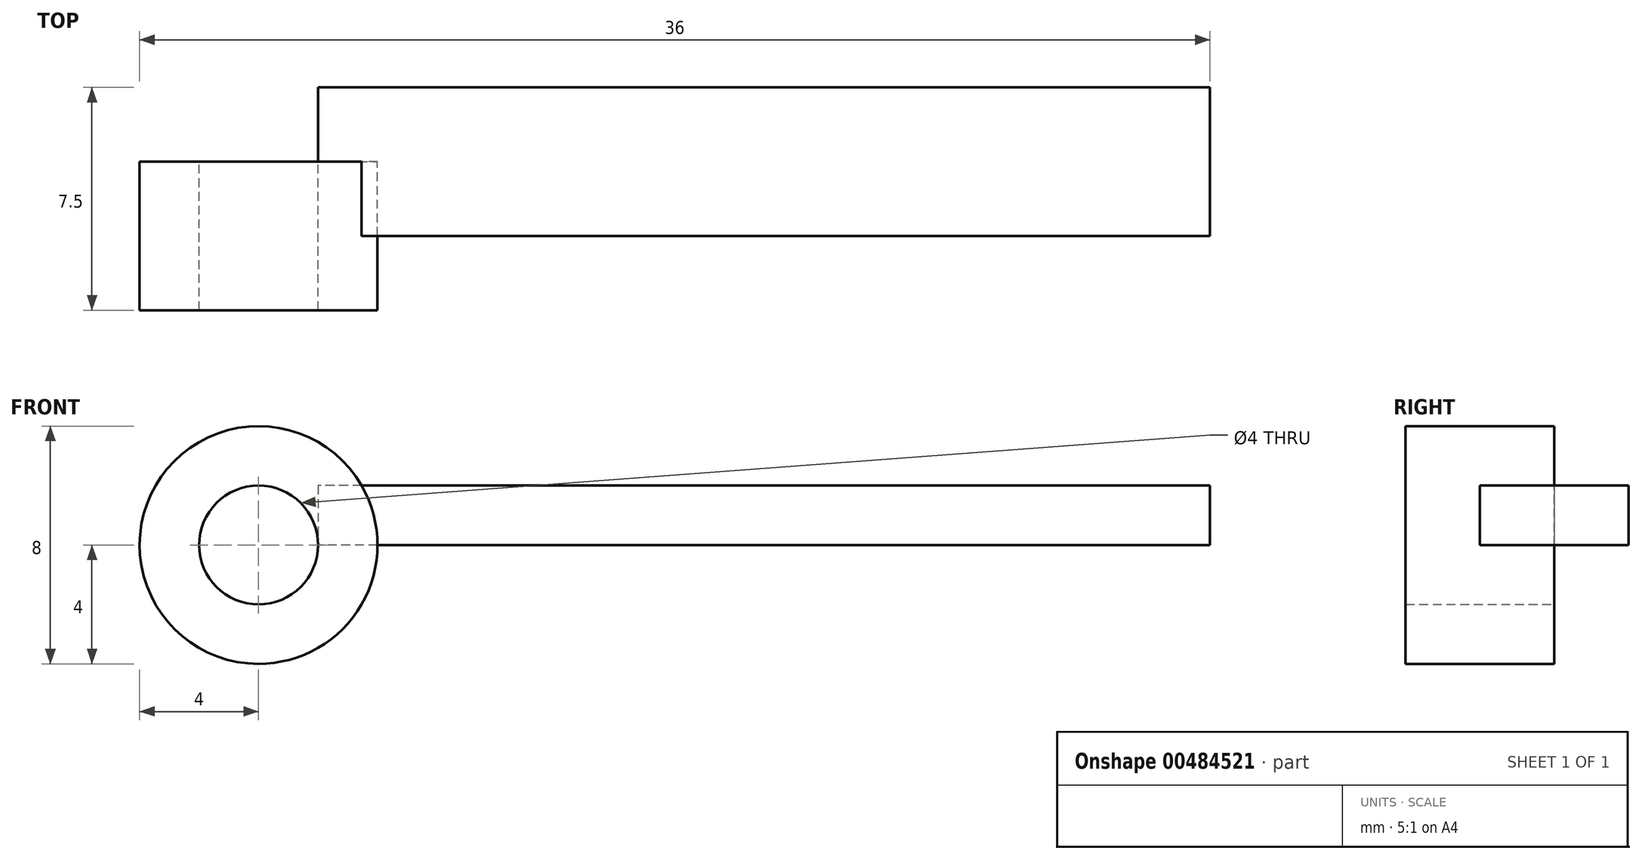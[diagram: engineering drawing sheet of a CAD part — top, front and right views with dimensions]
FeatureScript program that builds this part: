
annotation { "Feature Type Name" : "Feature", "Feature Type Description" : "" }
export const myFeature = defineFeature(function(context is Context, id is Id, definition is map)
    precondition{}
    {
        {
            var Q0;
            Q0=qCreatedBy(makeId("Top.planeOp"),FACE);
            var sketch = newSketch(context, id + "F0", { "sketchPlane" : qUnion([Q0])});
            skLineSegment(sketch, "E0.bottom", {"start": v(28, -2.5) * mm, "end": v(-2, -2.5) * mm});
            skLineSegment(sketch, "E0.top", {"start": v(28, 2.5) * mm, "end": v(-2, 2.5) * mm});
            skLineSegment(sketch, "E0.left", {"start": v(28, -2.5) * mm, "end": v(28, 2.5) * mm});
            skLineSegment(sketch, "E0.right", {"start": v(-2, -2.5) * mm, "end": v(-2, 2.5) * mm});
            skPoint(sketch, "E0.middle", {"position": v(13, 0) * mm});
            skSolve(sketch);
        }
        {
            var Q0;
            Q0=qCreatedBy(makeId("Front.planeOp"),FACE);
            var sketch = newSketch(context, id + "F1", { "sketchPlane" : qUnion([Q0])});
            skCircle(sketch, "E1", {"center": v(-4, 0) * mm, "radius": 4 * mm});
            skCircle(sketch, "E2", {"center": v(-4, 0) * mm, "radius": 2 * mm});
            skSolve(sketch);
        }
        {
            var Q0;
            Q0 = qSketchRegion(id + "F1", true);
            extrude(context, id + "F2", {"entities" : qUnion([Q0]), "depth" : 5 * mm});
        }
        {
            var Q0;
            Q0=makeQuery(id+"F0.imprint","IMPRINT",FACE,{"disambiguationData":[TD([[makeQuery(id+"F0.imprint","IMPRINT",EDGE,{"derivedFrom":sQuery(id+"F0.wireOp",EDGE,"E0.bottom")}),-1.0]])]});
            extrude(context, id + "F3", {"entities" : qUnion([Q0]), "operationType" : NewBodyOperationType.ADD, "depth" : 2 * mm});
        }
    });
